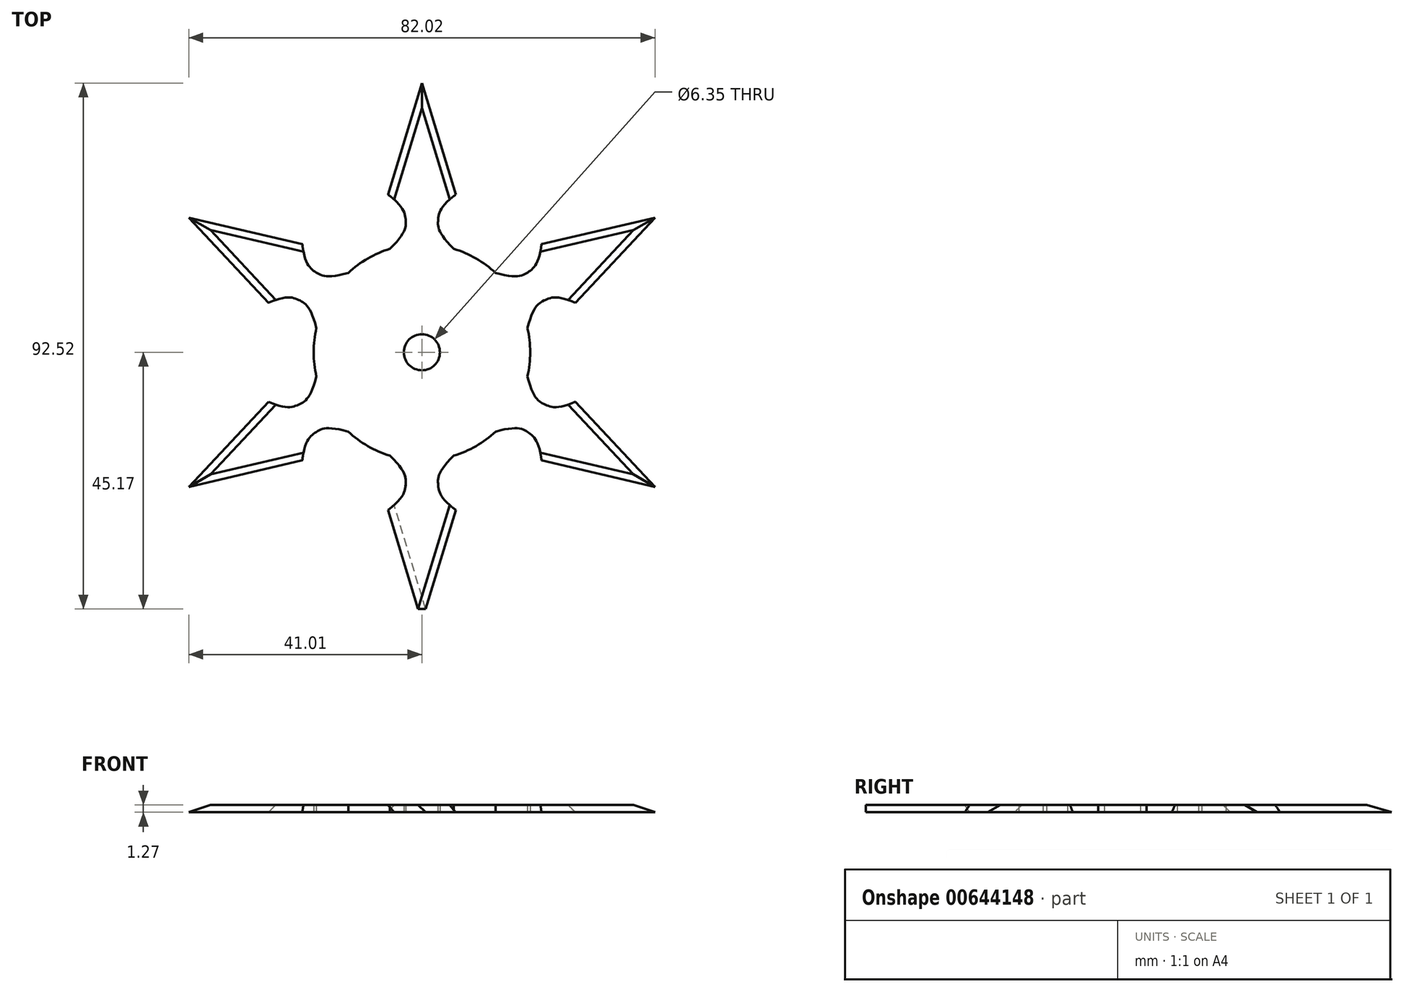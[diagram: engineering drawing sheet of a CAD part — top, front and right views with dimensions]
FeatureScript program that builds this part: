
annotation { "Feature Type Name" : "Feature", "Feature Type Description" : "" }
export const myFeature = defineFeature(function(context is Context, id is Id, definition is map)
    precondition{}
    {
        {
            var Q0;
            Q0=qCreatedBy(makeId("Top.planeOp"),FACE);
            var sketch = newSketch(context, id + "F0", { "sketchPlane" : qUnion([Q0])});
            skCircle(sketch, "E0", {"center": v(0, 0) * mm, "radius": 19.05 * mm});
            skCircle(sketch, "E1", {"center": v(0, 0) * mm, "radius": 3.18 * mm});
            skFitSpline(sketch, "E2.MirrorCS", {"points": [v(-5.6, 18.2) * mm, v(-2.86, 23.29) * mm, v(-6.09, 27.83) * mm], "startDerivative": vector(16.9, 16.58) * mm, "endDerivative": vector(-17.88, 12.85) * mm});
            skLineSegment(sketch, "E3", {"start": v(0, 0) * mm, "end": v(0, 50.22) * mm});
            skFitSpline(sketch, "E4.MirrorCS", {"points": [v(5.6, 18.2) * mm, v(2.86, 23.29) * mm, v(6.09, 27.83) * mm], "startDerivative": vector(-16.9, 16.58) * mm, "endDerivative": vector(17.88, 12.85) * mm});
            skLineSegment(sketch, "E5", {"start": v(-6.09, 27.83) * mm, "end": v(6.09, 27.83) * mm});
            skLineSegment(sketch, "E6", {"start": v(-6.09, 27.83) * mm, "end": v(0, 47.88) * mm});
            skLineSegment(sketch, "E7", {"start": v(0, 47.88) * mm, "end": v(6.09, 27.83) * mm});
            skSolve(sketch);
        }
        {
            var Q0;
            {var subQ0=sQuery(id+"F0.wireOp",EDGE,"E7");Q0=makeQuery(id+"F0.imprint","IMPRINT",FACE,{"disambiguationData":[TD([[makeQuery(id+"F0.imprint","IMPRINT",EDGE,{"derivedFrom":subQ0}),-1.0]])]});}
            var Q1;
            {var subQ0=sQuery(id+"F0.wireOp",EDGE,"E6");Q1=makeQuery(id+"F0.imprint","IMPRINT",FACE,{"disambiguationData":[TD([[makeQuery(id+"F0.imprint","IMPRINT",EDGE,{"derivedFrom":subQ0}),-1.0]])]});}
            var Q2;
            {var subQ0=sQuery(id+"F0.wireOp",EDGE,"E2.MirrorCS");Q2=makeQuery(id+"F0.imprint","IMPRINT",FACE,{"disambiguationData":[TD([[makeQuery(id+"F0.imprint","IMPRINT",EDGE,{"derivedFrom":subQ0}),-1.0]])]});}
            var Q3;
            {var subQ0=sQuery(id+"F0.wireOp",EDGE,"E4.MirrorCS");Q3=makeQuery(id+"F0.imprint","IMPRINT",FACE,{"disambiguationData":[TD([[makeQuery(id+"F0.imprint","IMPRINT",EDGE,{"derivedFrom":subQ0}),1.0]])]});}
            extrude(context, id + "F1", {"entities" : qUnion([Q0, Q1, Q2, Q3]), "depth" : 1.27 * mm, "offsetDistance" : 25.4 * mm});
        }
        {
            var Q0;
            Q0=makeQuery(id+"F1.opExtrude","SWEPT_BODY",BODY,{"disambiguationData":[OSD([sQuery(id+"F0.wireOp",EDGE,"E0"),sQuery(id+"F0.wireOp",EDGE,"E2.MirrorCS"),sQuery(id+"F0.wireOp",EDGE,"E4.MirrorCS"),sQuery(id+"F0.wireOp",EDGE,"E6"),sQuery(id+"F0.wireOp",EDGE,"E7")])]});
            var Q1;
            Q1=sQuery(id+"F0.wireOp",EDGE,"E1");
            circularPattern(context, id + "F2", {"entities" : qUnion([Q0]), "axis" : qUnion([Q1]), "angle" : 360 * degree, "instanceCount" : 6, "equalSpace" : true});
        }
        {
            var Q0;
            Q0=makeQuery(id+"F0.imprint","IMPRINT",FACE,{"disambiguationData":[TD([[makeQuery(id+"F0.imprint","IMPRINT",EDGE,{"derivedFrom":sQuery(id+"F0.wireOp",EDGE,"E1")}),-1.0]])]});
            extrude(context, id + "F3", {"entities" : qUnion([Q0]), "operationType" : NewBodyOperationType.ADD, "depth" : 1.27 * mm, "offsetDistance" : 25.4 * mm});
        }
        {
            var Q0;
            Q0=makeQuery(id+"F2.opPattern","COPY",EDGE,{"derivedFrom":makeQuery(id+"F1.opExtrude","CAP_EDGE",EDGE,{"disambiguationData":[OSD([sQuery(id+"F0.wireOp",EDGE,"E7")])],"isStart":false}),"instanceName":"1"});
            var Q1;
            Q1=makeQuery(id+"F2.opPattern","COPY",EDGE,{"derivedFrom":makeQuery(id+"F1.opExtrude","CAP_EDGE",EDGE,{"disambiguationData":[OSD([sQuery(id+"F0.wireOp",EDGE,"E6")])],"isStart":false}),"instanceName":"1"});
            var Q2;
            Q2=makeQuery(id+"F1.opExtrude","CAP_EDGE",EDGE,{"disambiguationData":[OSD([sQuery(id+"F0.wireOp",EDGE,"E6")])],"isStart":false});
            var Q3;
            Q3=makeQuery(id+"F1.opExtrude","CAP_EDGE",EDGE,{"disambiguationData":[OSD([sQuery(id+"F0.wireOp",EDGE,"E7")])],"isStart":false});
            var Q4;
            Q4=makeQuery(id+"F2.opPattern","COPY",EDGE,{"derivedFrom":makeQuery(id+"F1.opExtrude","CAP_EDGE",EDGE,{"disambiguationData":[OSD([sQuery(id+"F0.wireOp",EDGE,"E6")])],"isStart":false}),"instanceName":"5"});
            var Q5;
            Q5=makeQuery(id+"F2.opPattern","COPY",EDGE,{"derivedFrom":makeQuery(id+"F1.opExtrude","CAP_EDGE",EDGE,{"disambiguationData":[OSD([sQuery(id+"F0.wireOp",EDGE,"E7")])],"isStart":false}),"instanceName":"5"});
            var Q6;
            Q6=makeQuery(id+"F2.opPattern","COPY",EDGE,{"derivedFrom":makeQuery(id+"F1.opExtrude","CAP_EDGE",EDGE,{"disambiguationData":[OSD([sQuery(id+"F0.wireOp",EDGE,"E6")])],"isStart":false}),"instanceName":"4"});
            var Q7;
            Q7=makeQuery(id+"F2.opPattern","COPY",EDGE,{"derivedFrom":makeQuery(id+"F1.opExtrude","CAP_EDGE",EDGE,{"disambiguationData":[OSD([sQuery(id+"F0.wireOp",EDGE,"E7")])],"isStart":false}),"instanceName":"4"});
            var Q8;
            Q8=makeQuery(id+"F2.opPattern","COPY",EDGE,{"derivedFrom":makeQuery(id+"F1.opExtrude","CAP_EDGE",EDGE,{"disambiguationData":[OSD([sQuery(id+"F0.wireOp",EDGE,"E6")])],"isStart":false}),"instanceName":"3"});
            var Q9;
            Q9=makeQuery(id+"F2.opPattern","COPY",EDGE,{"derivedFrom":makeQuery(id+"F1.opExtrude","CAP_EDGE",EDGE,{"disambiguationData":[OSD([sQuery(id+"F0.wireOp",EDGE,"E7")])],"isStart":true}),"instanceName":"3"});
            var Q10;
            Q10=makeQuery(id+"F2.opPattern","COPY",EDGE,{"derivedFrom":makeQuery(id+"F1.opExtrude","CAP_EDGE",EDGE,{"disambiguationData":[OSD([sQuery(id+"F0.wireOp",EDGE,"E6")])],"isStart":false}),"instanceName":"2"});
            var Q11;
            Q11=makeQuery(id+"F2.opPattern","COPY",EDGE,{"derivedFrom":makeQuery(id+"F1.opExtrude","CAP_EDGE",EDGE,{"disambiguationData":[OSD([sQuery(id+"F0.wireOp",EDGE,"E7")])],"isStart":false}),"instanceName":"2"});
            chamfer(context, id + "F4", {"entities" : qUnion([Q0, Q1, Q2, Q3, Q4, Q5, Q6, Q7, Q8, Q9, Q10, Q11]), "width" : 1.42 * mm});
        }
    });
